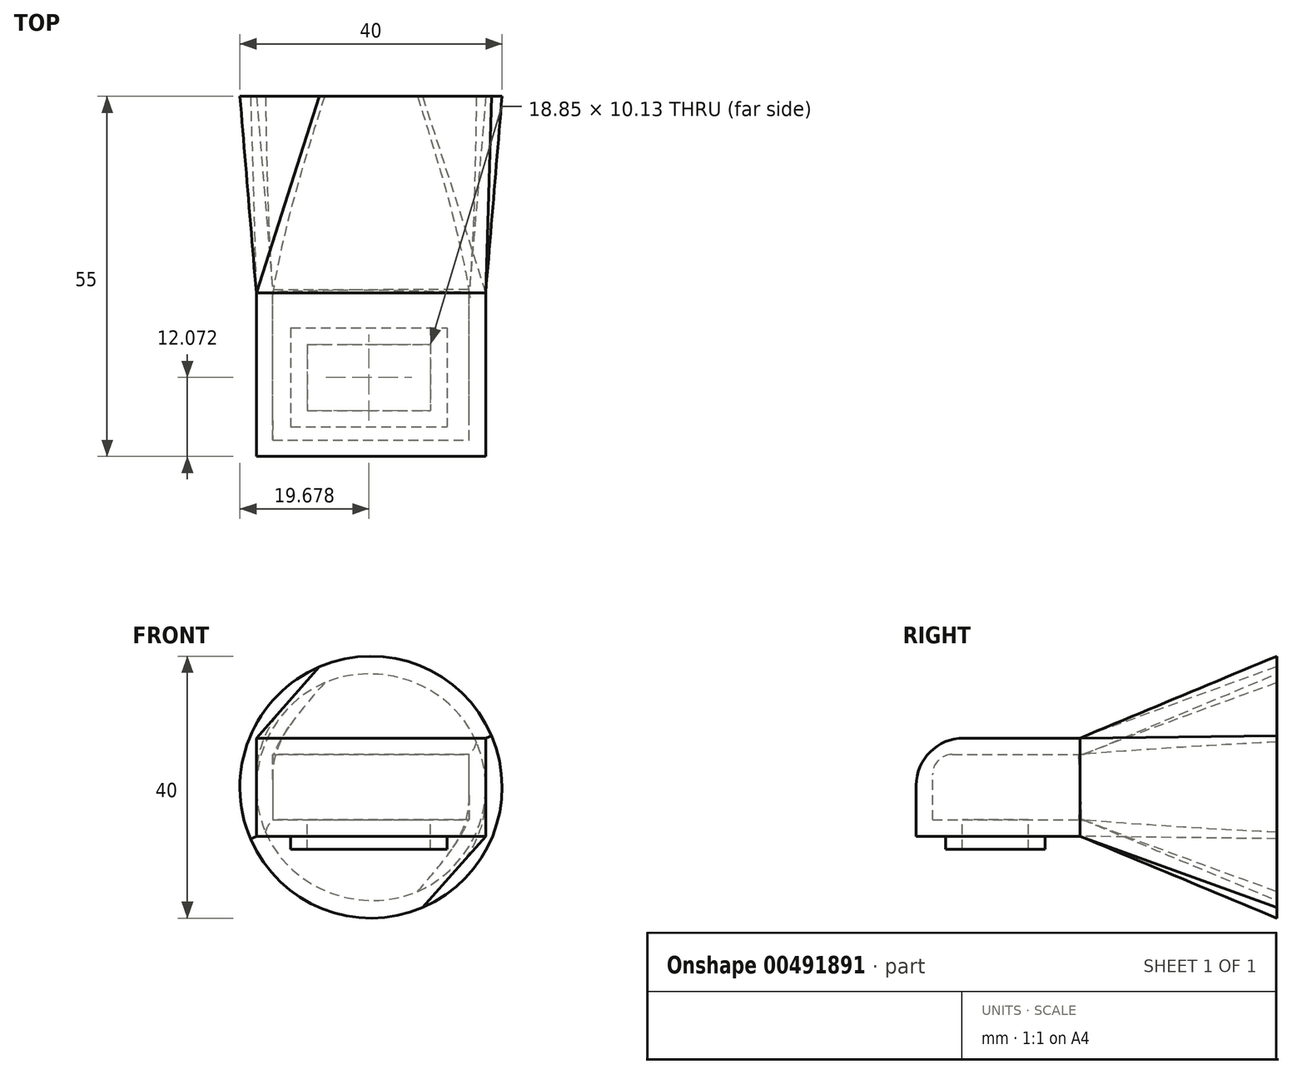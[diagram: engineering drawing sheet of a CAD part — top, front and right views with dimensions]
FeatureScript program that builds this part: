
annotation { "Feature Type Name" : "Feature", "Feature Type Description" : "" }
export const myFeature = defineFeature(function(context is Context, id is Id, definition is map)
    precondition{}
    {
        {
            var Q0;
            Q0=qCreatedBy(makeId("Front.planeOp"),FACE);
            var sketch = newSketch(context, id + "F0", { "sketchPlane" : qUnion([Q0])});
            skEllipse(sketch, "E0", {"center": v(0, 0) * mm, "majorRadius": 20 * mm, "minorRadius": 20 * mm, "majorAxis": v(1, -0.02)});
            skSolve(sketch);
        }
        {
            var Q0;
            Q0=qCreatedBy(makeId("Front.planeOp"),FACE);
            cPlane(context, id + "F1", {"entities" : qUnion([Q0]), "cplaneType" : CPlaneType.OFFSET, "offset" : 30 * mm, "width" : 150 * mm, "height" : 150 * mm});
        }
        {
            var Q0;
            Q0=qCreatedBy(id+"F1.planeOp",FACE);
            var sketch = newSketch(context, id + "F2", { "sketchPlane" : qUnion([Q0])});
            skLineSegment(sketch, "E1.bottom", {"start": v(17.5, 7.5) * mm, "end": v(-17.5, 7.5) * mm});
            skLineSegment(sketch, "E1.top", {"start": v(17.5, -7.5) * mm, "end": v(-17.5, -7.5) * mm});
            skLineSegment(sketch, "E1.left", {"start": v(17.5, 7.5) * mm, "end": v(17.5, -7.5) * mm});
            skLineSegment(sketch, "E1.right", {"start": v(-17.5, 7.5) * mm, "end": v(-17.5, -7.5) * mm});
            skPoint(sketch, "E1.middle", {"position": v(0, 0) * mm});
            skSolve(sketch);
        }
        {
            var Q0;
            Q0=qSketchRegion(id+"F0",true);
            var Q1;
            Q1=qSketchRegion(id+"F2",true);
            loft(context, id + "F3", {"sheetProfilesArray" : [{ "sheetProfileEntities" : qUnion([Q0]) }, { "sheetProfileEntities" : qUnion([Q1]) }]});
        }
        {
            var Q0;
            Q0=makeQuery(id+"F3.opLoft","CAP_FACE",FACE,{"disambiguationData":[OSD([makeQuery(id+"F2.imprint","IMPRINT",FACE,{"disambiguationData":[TD([[makeQuery(id+"F2.imprint","IMPRINT",EDGE,{"derivedFrom":sQuery(id+"F2.wireOp",EDGE,"E1.bottom")}),1.0]])]})])],"isStart":true});
            extrude(context, id + "F4", {"entities" : qUnion([Q0]), "operationType" : NewBodyOperationType.ADD, "depth" : 25 * mm});
        }
        {
            var Q0;
            Q0=makeQuery(id+"F4.opExtrude","SWEPT_FACE",FACE,{"disambiguationData":[OSD([sQuery(id+"F2.wireOp",EDGE,"E1.top"),sQuery(id+"F2.wireOp",EDGE,"E1.left"),sQuery(id+"F2.wireOp",EDGE,"E1.right")])]});
            var sketch = newSketch(context, id + "F5", { "sketchPlane" : qUnion([Q0])});
            skLineSegment(sketch, "E2.bottom", {"start": v(-12.25, 35.36) * mm, "end": v(11.6, 35.36) * mm});
            skLineSegment(sketch, "E2.top", {"start": v(-12.25, 50.5) * mm, "end": v(11.6, 50.5) * mm});
            skLineSegment(sketch, "E2.left", {"start": v(-12.25, 35.36) * mm, "end": v(-12.25, 50.5) * mm});
            skLineSegment(sketch, "E2.right", {"start": v(11.6, 35.36) * mm, "end": v(11.6, 50.5) * mm});
            skSolve(sketch);
        }
        {
            var Q0;
            Q0=qSketchRegion(id+"F5",true);
            extrude(context, id + "F6", {"entities" : qUnion([Q0]), "operationType" : NewBodyOperationType.ADD, "depth" : 2 * mm});
        }
        {
            var Q0;
            Q0=makeQuery(id+"F6.opExtrude","CAP_FACE",FACE,{"disambiguationData":[OSD([sQuery(id+"F5.wireOp",EDGE,"E2.bottom"),sQuery(id+"F5.wireOp",EDGE,"E2.top"),sQuery(id+"F5.wireOp",EDGE,"E2.left"),sQuery(id+"F5.wireOp",EDGE,"E2.right")])],"isStart":false});
            var Q1;
            Q1=makeQuery(id+"F3.opLoft","CAP_FACE",FACE,{"disambiguationData":[OSD([makeQuery(id+"F0.imprint","IMPRINT",FACE,{"disambiguationData":[TD([[makeQuery(id+"F0.imprint","IMPRINT",EDGE,{"derivedFrom":sQuery(id+"F0.wireOp",EDGE,"E0")}),1.0]])]})])],"isStart":true});
            var Q2;
            Q2=makeQuery(id+"F3.opLoft","SWEPT_BODY",BODY,{"disambiguationData":[OSD([makeQuery(id+"F0.imprint","IMPRINT",FACE,{"disambiguationData":[TD([[makeQuery(id+"F0.imprint","IMPRINT",EDGE,{"derivedFrom":sQuery(id+"F0.wireOp",EDGE,"E0")}),1.0]])]}),makeQuery(id+"F2.imprint","IMPRINT",FACE,{"disambiguationData":[TD([[makeQuery(id+"F2.imprint","IMPRINT",EDGE,{"derivedFrom":sQuery(id+"F2.wireOp",EDGE,"E1.bottom")}),1.0]])]})])]});
            shell(context, id + "F7", {"entities" : qUnion([Q0, Q1]), "parts" : qUnion([Q2]), "thickness" : 2.5 * mm});
        }
        {
            var Q0;
            Q0=makeQuery(id+"F4.opExtrude","CAP_EDGE",EDGE,{"disambiguationData":[OSD([sQuery(id+"F2.wireOp",EDGE,"E1.bottom"),sQuery(id+"F2.wireOp",EDGE,"E1.left"),sQuery(id+"F2.wireOp",EDGE,"E1.right")])],"isStart":false});
            fillet(context, id + "F8", {"entities" : qUnion([Q0]), "radius" : 7.23 * mm, "tangentPropagation" : true, "allowEdgeOverflow" : false});
        }
        {
            var Q0;
            {var subQ0=sQuery(id+"F2.wireOp",EDGE,"E1.right");var subQ1=sQuery(id+"F2.wireOp",EDGE,"E1.left");var subQ2=sQuery(id+"F2.wireOp",EDGE,"E1.bottom");Q0=makeQuery(id+"F7.opShell","OFFSET_EDGE",EDGE,{"disambiguationData":[OSD([subQ2,subQ1,subQ0]),TDD([makeQuery(id+"F4.opExtrude","CAP_EDGE",EDGE,{"disambiguationData":[OSD([subQ2,subQ1,subQ0])],"isStart":false})])]});}
            fillet(context, id + "F9", {"entities" : qUnion([Q0]), "radius" : 3 * mm, "tangentPropagation" : true, "allowEdgeOverflow" : false});
        }
    });
